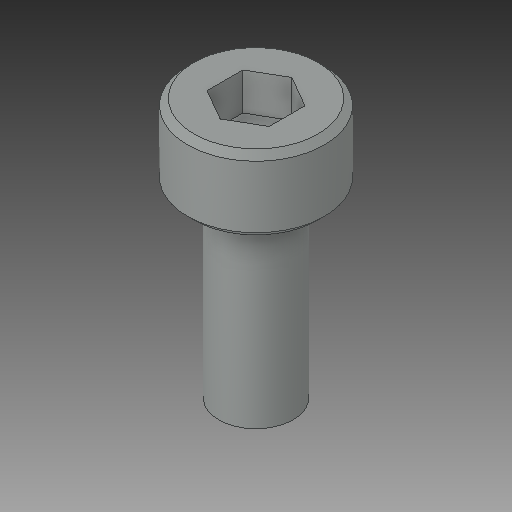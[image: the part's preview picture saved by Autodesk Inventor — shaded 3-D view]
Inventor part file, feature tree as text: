
AUTODESK INVENTOR PART (.ipt)
format: ipt  version: 2017 SP1 (Build 210196100, 196)  size: 106,496 bytes
history: native  units: in
note: dims shown in document units (in); Inventor stores cm internally (conversion verified against a paired STEP export)
features: chamfer x1
ambient origin geometry x8: Origin, YZ Plane, XZ Plane, XY Plane, X Axis, Y Axis, Z Axis, Center Point
bodies: Solid1 (feature_tree)
feature tree (1):
  chamfer  "Chamfer2"  [1 undecoded]
note: 1 required parameter value undecoded (feature->parameter linkage not recoverable at this tier; creation-order binding heuristic only, values carry confidence <= 0.55)
